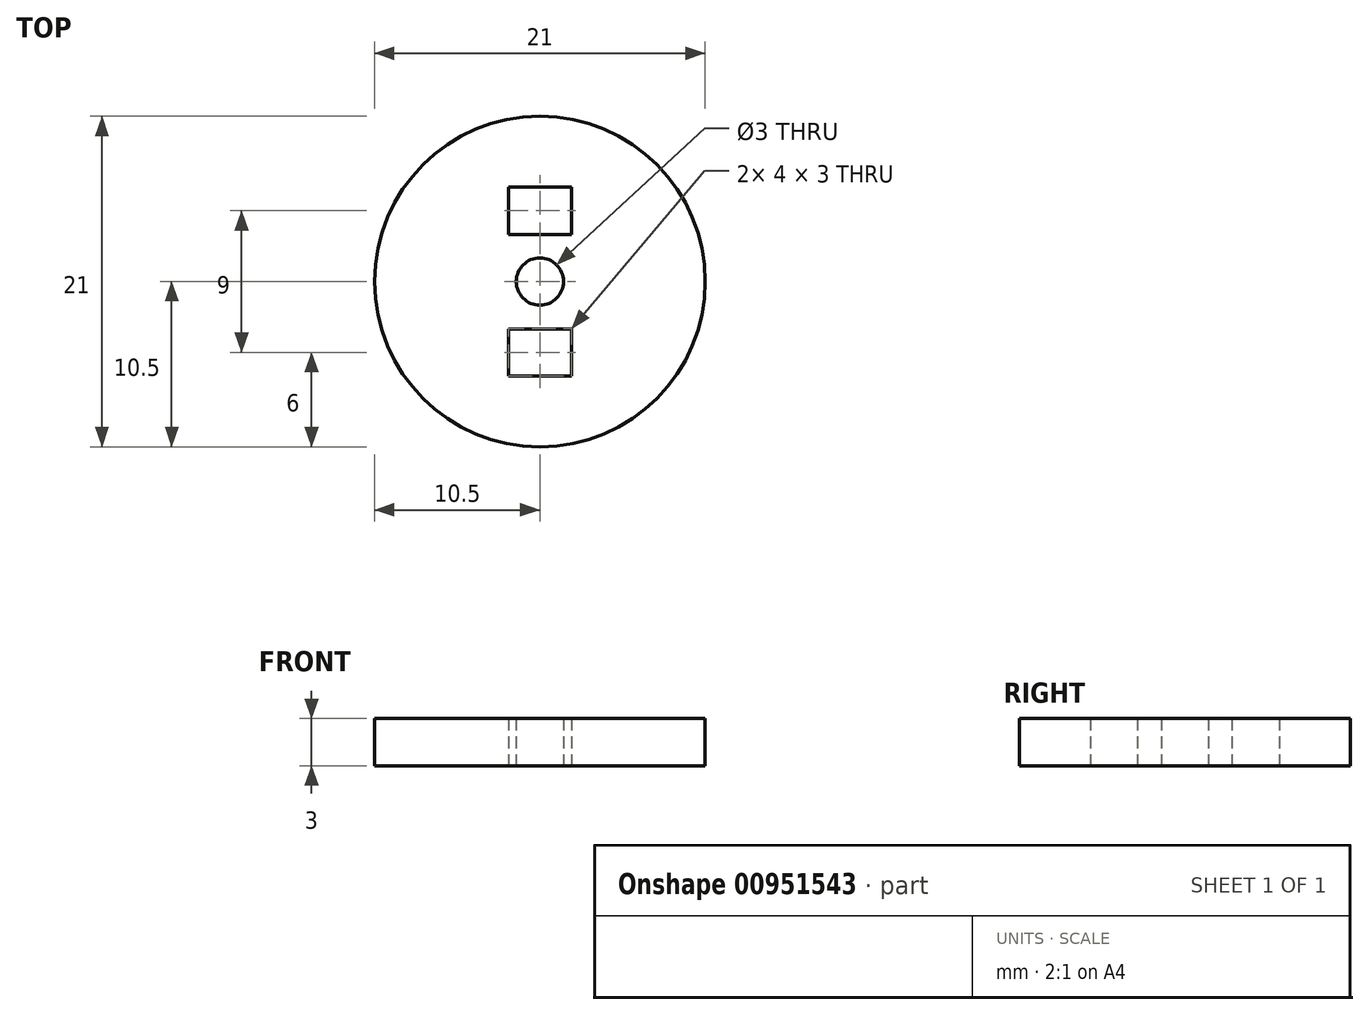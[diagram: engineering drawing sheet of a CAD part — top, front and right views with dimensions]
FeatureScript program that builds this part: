
annotation { "Feature Type Name" : "Feature", "Feature Type Description" : "" }
export const myFeature = defineFeature(function(context is Context, id is Id, definition is map)
    precondition{}
    {
        {
            var Q0;
            Q0=qCreatedBy(makeId("Top.planeOp"),FACE);
            var sketch = newSketch(context, id + "F0", { "sketchPlane" : qUnion([Q0])});
            skCircle(sketch, "E0", {"center": v(0, 0) * mm, "radius": 10.5 * mm});
            skCircle(sketch, "E1", {"center": v(0, 0) * mm, "radius": 1.5 * mm});
            skLineSegment(sketch, "E2.bottom", {"start": v(-2, 3) * mm, "end": v(2, 3) * mm});
            skLineSegment(sketch, "E2.top", {"start": v(-2, 6) * mm, "end": v(2, 6) * mm});
            skLineSegment(sketch, "E2.left", {"start": v(-2, 3) * mm, "end": v(-2, 6) * mm});
            skLineSegment(sketch, "E2.right", {"start": v(2, 3) * mm, "end": v(2, 6) * mm});
            skPoint(sketch, "E2.middle", {"position": v(0, 4.5) * mm});
            skLineSegment(sketch, "E3.bottom", {"start": v(-2, -6) * mm, "end": v(2, -6) * mm});
            skLineSegment(sketch, "E3.top", {"start": v(-2, -3) * mm, "end": v(2, -3) * mm});
            skLineSegment(sketch, "E3.left", {"start": v(-2, -6) * mm, "end": v(-2, -3) * mm});
            skLineSegment(sketch, "E3.right", {"start": v(2, -6) * mm, "end": v(2, -3) * mm});
            skPoint(sketch, "E3.middle", {"position": v(0, -4.5) * mm});
            skSolve(sketch);
        }
        {
            var Q0;
            Q0=qSketchRegion(id+"F0",true);
            extrude(context, id + "F1", {"entities" : qUnion([Q0]), "depth" : 3 * mm, "offsetDistance" : 25 * mm});
        }
        {
            var Q0;
            Q0 = qSketchRegion(id + "F0", true);
            extrude(context, id + "F2", {"entities" : qUnion([Q0]), "operationType" : NewBodyOperationType.ADD, "depth" : 3 * mm, "offsetDistance" : 25 * mm});
        }
    });
